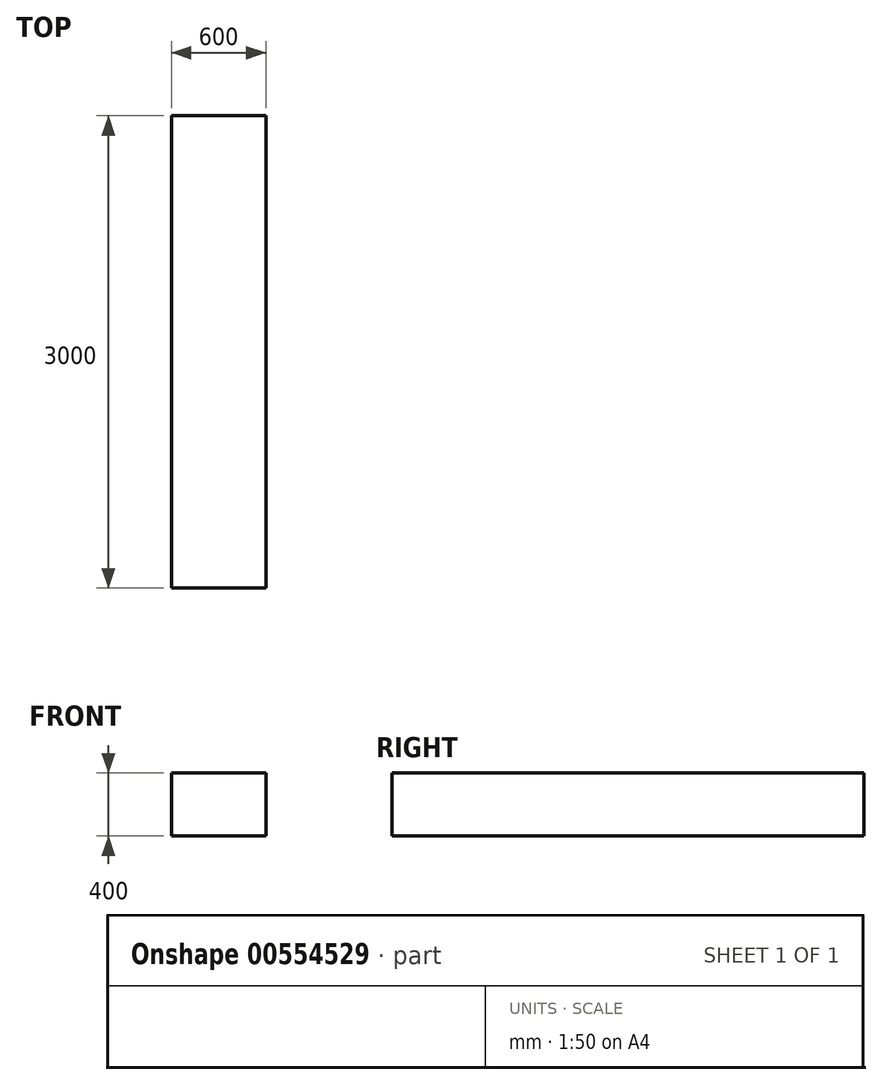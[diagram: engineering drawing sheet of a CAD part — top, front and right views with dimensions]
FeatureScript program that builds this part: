
annotation { "Feature Type Name" : "Feature", "Feature Type Description" : "" }
export const myFeature = defineFeature(function(context is Context, id is Id, definition is map)
    precondition{}
    {
        {
            var Q0;
            Q0=qCreatedBy(makeId("Front.planeOp"),FACE);
            var sketch = newSketch(context, id + "F0", { "sketchPlane" : qUnion([Q0])});
            skLineSegment(sketch, "E0.bottom", {"start": v(0, 0) * mm, "end": v(600, 0) * mm});
            skLineSegment(sketch, "E0.top", {"start": v(0, -400) * mm, "end": v(600, -400) * mm});
            skLineSegment(sketch, "E0.left", {"start": v(0, 0) * mm, "end": v(0, -400) * mm});
            skLineSegment(sketch, "E0.right", {"start": v(600, 0) * mm, "end": v(600, -400) * mm});
            skSolve(sketch);
        }
        {
            var Q0;
            Q0=makeQuery(id+"F0.imprint","IMPRINT",FACE,{"disambiguationData":[TD([[makeQuery(id+"F0.imprint","IMPRINT",EDGE,{"derivedFrom":sQuery(id+"F0.wireOp",EDGE,"E0.bottom")}),-1.0]])]});
            extrude(context, id + "F1", {"entities" : qUnion([Q0]), "depth" : 3000 * mm, "offsetDistance" : 25 * mm});
        }
    });
